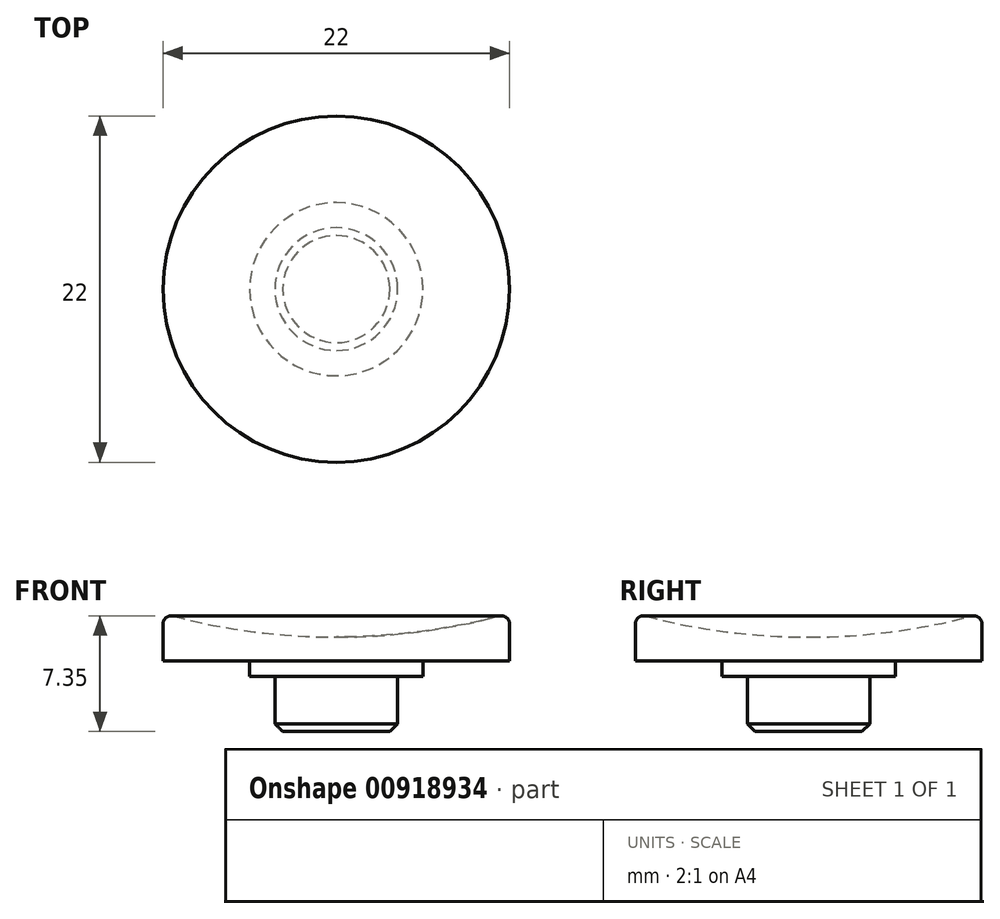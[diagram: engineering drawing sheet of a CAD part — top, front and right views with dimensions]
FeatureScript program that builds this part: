
annotation { "Feature Type Name" : "Feature", "Feature Type Description" : "" }
export const myFeature = defineFeature(function(context is Context, id is Id, definition is map)
    precondition{}
    {
        {
            var Q0;
            Q0=qCreatedBy(makeId("Front.planeOp"),FACE);
            var sketch = newSketch(context, id + "F0", { "sketchPlane" : qUnion([Q0])});
            skLineSegment(sketch, "E0", {"start": v(0, 0) * mm, "end": v(0, 17.65) * mm, "construction": true});
            skLineSegment(sketch, "E1", {"start": v(0, 0) * mm, "end": v(3.9, 0) * mm});
            skLineSegment(sketch, "E2", {"start": v(3.9, 0) * mm, "end": v(3.9, 3.5) * mm});
            skLineSegment(sketch, "E3", {"start": v(3.9, 3.5) * mm, "end": v(5.5, 3.5) * mm});
            skLineSegment(sketch, "E4", {"start": v(5.5, 3.5) * mm, "end": v(5.5, 4.5) * mm});
            skLineSegment(sketch, "E5", {"start": v(5.5, 4.5) * mm, "end": v(11, 4.5) * mm});
            skLineSegment(sketch, "E6", {"start": v(11, 4.5) * mm, "end": v(11, 7.5) * mm});
            skArc(sketch, "E7", {"start": v(11, 7.5) * mm, "mid": v(5.55, 6.38) * mm, "end": v(0, 6) * mm});
            skLineSegment(sketch, "E8", {"start": v(0, 6) * mm, "end": v(0, 0) * mm});
            skSolve(sketch);
        }
        {
            var Q0;
            Q0 = qSketchRegion(id + "F0", true);
            var Q1;
            Q1=sQuery(id+"F0.wireOp",EDGE,"E0");
            revolve(context, id + "F1", {"surfaceOperationType" : NewSurfaceOperationType.NEW, "entities" : qUnion([Q0]), "axis" : qUnion([Q1]), "revolveType" : RevolveType.FULL});
        }
        {
            var Q0;
            Q0=makeQuery(id+"F1.opRevolve","SWEPT_EDGE",EDGE,{"disambiguationData":[OSD([sQuery(id+"F0.wireOp",EDGE,"E1"),sQuery(id+"F0.wireOp",EDGE,"E2")])]});
            chamfer(context, id + "F2", {"entities" : qUnion([Q0]), "width" : 0.5 * mm, "tangentPropagation" : true});
        }
        {
            var Q0;
            Q0=makeQuery(id+"F1.opRevolve","SWEPT_EDGE",EDGE,{"disambiguationData":[OSD([sQuery(id+"F0.wireOp",EDGE,"E6"),sQuery(id+"F0.wireOp",EDGE,"E7")])]});
            fillet(context, id + "F3", {"entities" : qUnion([Q0]), "radius" : 0.5 * mm, "tangentPropagation" : true, "allowEdgeOverflow" : false});
        }
    });
